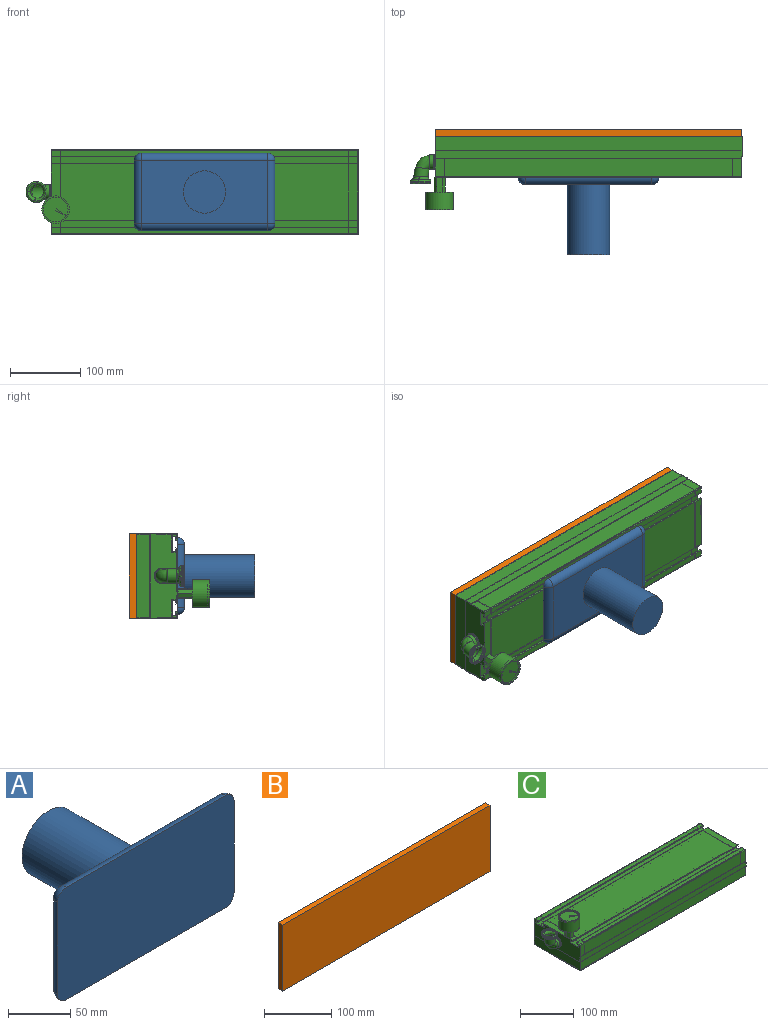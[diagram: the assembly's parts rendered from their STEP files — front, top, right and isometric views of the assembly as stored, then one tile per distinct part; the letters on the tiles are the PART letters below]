
ASSEMBLY  parts=3 mates=2
PART A: 12 faces, bbox 200x110x110 mm
  f0: plane 200x110mm, normal (0,-1,0), area 21914.2mm2, adj f4,f5,f6,f7,f8,f9,f10,f11
  f1: plane 180x90mm, normal (0,1,0), area 13372.6mm2, adj f2,f5,f6,f9,f10
  f2: cylinder r=30mm len=100mm, axis (0,-1,0), area 18849.6mm2, adj f1,f3
  f3: plane 60x60mm, normal (0,1,0), area 2827.4mm2, adj f2
  f4: sphere r=10mm, area 157.1mm2, adj f0,f5,f6
  f5: cylinder r=10mm len=90mm, axis (0,0,-1), area 1413.7mm2, adj f0,f1,f4,f7
  f6: cylinder r=10mm len=180mm, axis (1,0,0), area 2827.4mm2, adj f0,f1,f4,f8
  f7: sphere r=10mm, area 157.1mm2, adj f0,f5,f9
  f8: sphere r=10mm, area 157.1mm2, adj f0,f6,f10
  f9: cylinder r=10mm len=180mm, axis (-1,0,0), area 2827.4mm2, adj f0,f1,f7,f11
  f10: cylinder r=10mm len=90mm, axis (0,0,1), area 1413.7mm2, adj f0,f1,f8,f11
  f11: sphere r=10mm, area 157.1mm2, adj f0,f9,f10
PART B: 6 faces, bbox 435x10x120 mm
  f0: plane 435x10mm, normal (0,0,-1), area 4350mm2, adj f1,f3,f4,f5
  f1: plane 120x10mm, normal (1,0,0), area 1200mm2, adj f0,f2,f4,f5
  f2: plane 435x10mm, normal (0,0,1), area 4350mm2, adj f1,f3,f4,f5
  f3: plane 120x10mm, normal (-1,0,0), area 1200mm2, adj f0,f2,f4,f5
  f4: plane 435x120mm, normal (0,-1,0), area 52200mm2, adj f0,f1,f2,f3
  f5: plane 435x120mm, normal (0,1,0), area 52200mm2, adj f0,f1,f2,f3
PART C: 229 faces, bbox 472.5x122x104.6 mm
  f0: torus R=10mm, axis (0,1,0), area 808.9mm2, adj f5,f6
  f1: torus R=12.85mm, axis (0,0,1), area 133.1mm2, adj f4,f8
  f2: torus R=12mm, axis (1,0,0), area 148.1mm2, adj f5,f7
  f3: bspline ~13.12x11.53mm, area 103.6mm2, adj f6,f225,f226,f227
  f4: cylinder r=13.85mm len=27.7mm, axis (0,0,-1), area 117.2mm2, adj f1,f227,f228
  f5: cylinder r=9mm len=18mm, axis (1,0,0), area 326.2mm2, adj f0,f2
  f6: cylinder r=9mm len=19.81mm, axis (-0.14,0,0.99), area 692.2mm2, adj f0,f3,f225,f226
  f7: cylinder r=10mm len=20mm, axis (1,0,0), area 94mm2, adj f2,f126
  f8: cylinder r=12.85mm len=25.7mm, axis (0,0,1), area 80.7mm2, adj f1,f10
  f9: cylinder r=18.5mm len=37mm, axis (0,0,-1), area 2382.9mm2, adj f138,f204
  f10: torus R=12.85mm, axis (0,0,1), area 278.8mm2, adj f8,f13
  f11: torus R=12mm, axis (1,0,0), area 136.1mm2, adj f14,f16
  f12: bspline ~13.39x11.55mm, area 92.1mm2, adj f15,f122,f123,f124
  f13: cylinder r=14.85mm len=29.7mm, axis (0,0,-1), area 127.2mm2, adj f10,f124,f125
  f14: cylinder r=10mm len=20mm, axis (1,0,0), area 362.4mm2, adj f11,f121
  f15: cylinder r=10mm len=21.79mm, axis (-0.14,0,0.99), area 769.1mm2, adj f12,f121,f122,f123
  f16: cylinder r=11mm len=22mm, axis (1,0,0), area 69.1mm2, adj f11,f19
  f17: cylinder r=17.55mm len=35.1mm, axis (0,0,1), area 275.7mm2, adj f31,f98
  f18: cylinder r=19.5mm len=39mm, axis (0,0,-1), area 3063.1mm2, adj f97,f98
  f19: plane 121.1x38.6mm, normal (-1,0,0), area 4001.3mm2, adj f16,f22,f24,f28,f32,f33,f51,f52
  f20: plane 120.2x26.6mm, normal (1,0,0), area 24.8mm2, adj f23,f24,f27,f28,f32,f33,f34,f35
  f21: plane 120.2x26.6mm, normal (-1,0,0), area 24.8mm2, adj f23,f25,f27,f29,f34,f35,f36,f37
  f22: plane 120.15x0.1mm, normal (0,0,1), area 12mm2, adj f19,f85,f86,f110
  f23: plane 409.5x25mm, normal (0,1,0), area 10237.5mm2, adj f20,f21,f103,f113
  f24: plane 28.1x13mm, normal (0,1,0), area 328.2mm2, adj f19,f20,f105,f113,f117
  f25: plane 27.33x13mm, normal (0,1,0), area 328mm2, adj f21,f26,f108,f113,f118
  f26: plane 121.1x38.6mm, normal (1,0,0), area 4381.4mm2, adj f25,f29,f30,f67,f68,f69,f70,f71
  f27: plane 409.5x25mm, normal (0,-1,0), area 10237.5mm2, adj f20,f21,f104,f109
  f28: plane 27.33x13mm, normal (0,-1,0), area 328mm2, adj f19,f20,f106,f109,f120
  f29: plane 28.1x13mm, normal (0,-1,0), area 328.2mm2, adj f21,f26,f107,f109,f119
  f30: plane 120.15x0.1mm, normal (0,0,1), area 12mm2, adj f26,f84,f87,f116
  f31: plane 35.1x35.1mm, normal (0,0,1), area 942.1mm2, adj f17,f99,f100,f101
  f32: plane 62.26x13mm, normal (0,0,1), area 764.5mm2, adj f19,f20,f59,f91,f92,f93
  f33: plane 13x12.26mm, normal (0,0,1), area 114.5mm2, adj f19,f20,f58,f90,f94,f95
  f34: plane 409.5x79.8mm, normal (0,0,1), area 32678.1mm2, adj f20,f21,f37,f45
  f35: plane 409.5x8.4mm, normal (0,0,1), area 3439.8mm2, adj f20,f21,f46,f104
  f36: plane 409.5x8.4mm, normal (0,0,1), area 3439.8mm2, adj f20,f21,f43,f103
  f37: plane 409.5x2.5mm, normal (0,1,0), area 1023.8mm2, adj f20,f21,f34,f38
  f38: plane 409.5x5.15mm, normal (0,0,-1), area 2108.9mm2, adj f20,f21,f37,f39
  f39: plane 409.5x5.2mm, normal (0,0.99,-0.14), area 2151.4mm2, adj f20,f21,f38,f40
  f40: plane 409.5x22mm, normal (0,0,1), area 9009mm2, adj f20,f21,f39,f41
  f41: plane 409.5x5.2mm, normal (0,-0.99,-0.14), area 2151.4mm2, adj f20,f21,f40,f42
  f42: plane 409.5x5.15mm, normal (0,0,-1), area 2108.9mm2, adj f20,f21,f41,f43
  f43: plane 409.5x2.5mm, normal (0,-1,0), area 1023.8mm2, adj f20,f21,f36,f42
  f44: plane 409.5x5.15mm, normal (0,0,-1), area 2108.9mm2, adj f20,f21,f45,f50
  f45: plane 409.5x2.5mm, normal (0,-1,0), area 1023.8mm2, adj f20,f21,f34,f44
  f46: plane 409.5x2.5mm, normal (0,1,0), area 1023.8mm2, adj f20,f21,f35,f47
  f47: plane 409.5x5.15mm, normal (0,0,-1), area 2108.9mm2, adj f20,f21,f46,f48
  f48: plane 409.5x5.2mm, normal (0,0.99,-0.14), area 2151.4mm2, adj f20,f21,f47,f49
  f49: plane 409.5x22mm, normal (0,0,1), area 9009mm2, adj f20,f21,f48,f50
  f50: plane 409.5x5.2mm, normal (0,-0.99,-0.14), area 2151.4mm2, adj f20,f21,f44,f49
  f51: plane 13x8.6mm, normal (0,0,1), area 111.8mm2, adj f19,f20,f52,f106
  f52: plane 13x2.7mm, normal (0,1,0), area 35.1mm2, adj f19,f20,f51,f53
  f53: plane 13x5.16mm, normal (0,0,-1), area 67.1mm2, adj f19,f20,f52,f54
  f54: plane 13x5mm, normal (0,0.99,-0.14), area 65.7mm2, adj f19,f20,f53,f55
  f55: plane 21.77x13mm, normal (0,0,1), area 283mm2, adj f19,f20,f54,f56
  f56: plane 13x5mm, normal (0,-0.99,-0.14), area 65.7mm2, adj f19,f20,f55,f57
  f57: plane 13x5.16mm, normal (0,0,-1), area 67.1mm2, adj f19,f20,f56,f58
  f58: plane 13x2.7mm, normal (0,-1,0), area 35.1mm2, adj f19,f20,f33,f57
  f59: plane 13x2.7mm, normal (0,1,0), area 35.1mm2, adj f19,f20,f32,f60
  f60: plane 13x5.16mm, normal (0,0,-1), area 67.1mm2, adj f19,f20,f59,f61
  f61: plane 13x5mm, normal (0,0.99,-0.14), area 65.7mm2, adj f19,f20,f60,f62
  f62: plane 21.77x13mm, normal (0,0,1), area 283mm2, adj f19,f20,f61,f63
  f63: plane 13x5mm, normal (0,-0.99,-0.14), area 65.7mm2, adj f19,f20,f62,f64
  f64: plane 13x5.16mm, normal (0,0,-1), area 67.1mm2, adj f19,f20,f63,f65
  f65: plane 13x2.7mm, normal (0,-1,0), area 35.1mm2, adj f19,f20,f64,f66
  f66: plane 13x8.6mm, normal (0,0,1), area 111.8mm2, adj f19,f20,f65,f105
  f67: plane 13x8.6mm, normal (0,0,1), area 111.8mm2, adj f21,f26,f68,f108
  f68: plane 13x2.7mm, normal (0,-1,0), area 35.1mm2, adj f21,f26,f67,f69
  f69: plane 13x5.16mm, normal (0,0,-1), area 67.1mm2, adj f21,f26,f68,f70
  f70: plane 13x5mm, normal (0,-0.99,-0.14), area 65.7mm2, adj f21,f26,f69,f71
  f71: plane 21.77x13mm, normal (0,0,1), area 283mm2, adj f21,f26,f70,f72
  f72: plane 13x5mm, normal (0,0.99,-0.14), area 65.7mm2, adj f21,f26,f71,f73
  f73: plane 13x5.16mm, normal (0,0,-1), area 67.1mm2, adj f21,f26,f72,f74
  f74: plane 13x2.7mm, normal (0,1,0), area 35.1mm2, adj f21,f26,f73,f75
  f75: plane 80x13mm, normal (0,0,1), area 1040mm2, adj f21,f26,f74,f76
  f76: plane 13x2.7mm, normal (0,-1,0), area 35.1mm2, adj f21,f26,f75,f77
  f77: plane 13x5.16mm, normal (0,0,-1), area 67.1mm2, adj f21,f26,f76,f78
  f78: plane 13x5mm, normal (0,-0.99,-0.14), area 65.7mm2, adj f21,f26,f77,f79
  f79: plane 21.77x13mm, normal (0,0,1), area 283mm2, adj f21,f26,f78,f80
  f80: plane 13x5mm, normal (0,0.99,-0.14), area 65.7mm2, adj f21,f26,f79,f81
  f81: plane 13x5.16mm, normal (0,0,-1), area 67.1mm2, adj f21,f26,f80,f82
  f82: plane 13x2.7mm, normal (0,1,0), area 35.1mm2, adj f21,f26,f81,f83
  f83: plane 13x8.6mm, normal (0,0,1), area 111.8mm2, adj f21,f26,f82,f107
  f84: plane 435.7x20mm, normal (0,-1,0), area 8714mm2, adj f30,f85,f87,f88,f111
  f85: plane 121.15x29mm, normal (-1,0,0), area 2415mm2, adj f22,f84,f86,f88,f110,f111,f112,f120
  f86: plane 435.7x20mm, normal (0,1,0), area 8714mm2, adj f22,f85,f87,f88,f114
  f87: plane 121.15x29mm, normal (1,0,0), area 2415mm2, adj f30,f84,f86,f88,f114,f115,f116,f118
  f88: plane 435.7x120.3mm, normal (0,0,-1), area 52414.7mm2, adj f84,f85,f86,f87
  f89: plane 5.48x1.58mm, normal (0,0,-1), area 4.3mm2, adj f20,f90,f91
  f90: plane 21x7mm, normal (0.87,-0.5,0), area 169.7mm2, adj f33,f89,f91,f95,f97
  f91: plane 21x7mm, normal (0.87,0.5,0), area 169.7mm2, adj f32,f89,f90,f92,f97
  f92: plane 21x8.08mm, normal (0,1,0), area 169.7mm2, adj f32,f91,f93,f97
  f93: plane 21x7mm, normal (-0.87,0.5,0), area 169.7mm2, adj f32,f92,f94,f96,f97
  f94: plane 21x7mm, normal (-0.87,-0.5,0), area 169.7mm2, adj f33,f93,f95,f96,f97
  f95: plane 21x8.08mm, normal (0,-1,0), area 169.7mm2, adj f33,f90,f94,f97
  f96: plane 5.48x1.58mm, normal (0,0,-1), area 4.3mm2, adj f19,f93,f94
  f97: plane 39x39mm, normal (0,0,-1), area 1024.8mm2, adj f18,f90,f91,f92,f93,f94,f95
  f98: plane 39x39mm, normal (0,0,1), area 227mm2, adj f17,f18
  f99: plane 13.97x9.81mm, normal (0.57,0.82,0), area 17.1mm2, adj f31,f100,f101,f102
  f100: plane 2.6x1.5mm, normal (-0.87,0.5,0), area 3mm2, adj f31,f99,f101,f102
  f101: plane 15.47x7.21mm, normal (-0.42,-0.91,0), area 17.1mm2, adj f31,f99,f100,f102
  f102: plane 15.47x9.81mm, normal (0,0,1), area 25.5mm2, adj f99,f100,f101
  f103: cylinder r=1.5mm len=409.5mm, axis (-1,0,0), area 964.9mm2, adj f20,f21,f23,f36
  f104: cylinder r=1.5mm len=409.5mm, axis (-1,0,0), area 964.9mm2, adj f20,f21,f27,f35
  f105: cylinder r=1.5mm len=13mm, axis (1,0,0), area 30.6mm2, adj f19,f20,f24,f66
  f106: cylinder r=1.5mm len=13mm, axis (1,0,0), area 30.6mm2, adj f19,f20,f28,f51
  f107: cylinder r=1.5mm len=13mm, axis (-1,0,0), area 30.6mm2, adj f21,f26,f29,f83
  f108: cylinder r=1.5mm len=13mm, axis (-1,0,0), area 30.6mm2, adj f21,f25,f26,f67
  f109: plane 429.6x1mm, normal (0,0,1), area 427.6mm2, adj f20,f21,f27,f28,f29,f112,f119,f120
  f110: plane 9.77x0.1mm, normal (0,1,0), area 1mm2, adj f19,f22,f85,f120
  f111: plane 435.6x0.85mm, normal (0,0,-1), area 370.3mm2, adj f26,f84,f85,f112
  f112: plane 435.6x12mm, normal (0,-1,0), area 5223.3mm2, adj f26,f85,f109,f111,f119,f120
  f113: plane 429.6x1mm, normal (0,0,1), area 427.6mm2, adj f20,f21,f23,f24,f25,f115,f117,f118
  f114: plane 435.6x0.85mm, normal (0,0,-1), area 370.3mm2, adj f19,f86,f87,f115
  f115: plane 435.6x12mm, normal (0,1,0), area 5223.3mm2, adj f19,f87,f113,f114,f117,f118
  f116: plane 9.77x0.1mm, normal (0,-1,0), area 1mm2, adj f26,f30,f87,f118
  f117: cylinder r=3mm len=3mm, axis (0,1,0), area 4.2mm2, adj f19,f24,f113,f115
  f118: cylinder r=3mm len=3mm, axis (0,-1,0), area 4.3mm2, adj f25,f26,f87,f113,f115,f116
  f119: cylinder r=3mm len=3mm, axis (0,-1,0), area 4.2mm2, adj f26,f29,f109,f112
  f120: cylinder r=3mm len=3mm, axis (0,1,0), area 4.3mm2, adj f19,f28,f85,f109,f110,f112
  f121: torus R=10mm, axis (0,1,0), area 875.4mm2, adj f14,f15
  f122: bspline ~13.39x11.55mm, area 92.1mm2, adj f12,f15,f123,f124
  f123: bspline ~27.36x16.46mm, area 249.4mm2, adj f12,f15,f122,f125
  f124: bspline ~29.12x12.18mm, area 103.8mm2, adj f12,f13,f122,f125
  f125: bspline ~29.69x17.76mm, area 121.5mm2, adj f13,f123,f124
  f126: plane 120x40.6mm, normal (1,0,0), area 3933.5mm2, adj f7,f129,f131,f135,f139,f140,f158,f159
  f127: plane 118.2x28.6mm, normal (-1,0,0), area 34.6mm2, adj f130,f131,f134,f135,f139,f140,f141,f142
  f128: plane 118.2x26.6mm, normal (1,0,0), area 24.7mm2, adj f130,f132,f134,f136,f141,f142,f143,f144
  f129: plane 118.3x0.1mm, normal (0,0,-1), area 11.8mm2, adj f126,f191,f192,f193
  f130: plane 411.5x26mm, normal (0,-1,0), area 10699mm2, adj f127,f128,f209,f218
  f131: plane 28.1x11mm, normal (0,-1,0), area 288mm2, adj f126,f127,f211,f218,f221
  f132: plane 27.48x11mm, normal (0,-1,0), area 287.8mm2, adj f128,f133,f214,f218,f222
  f133: plane 120x38.6mm, normal (-1,0,0), area 4237.8mm2, adj f132,f136,f137,f174,f175,f176,f177,f178
  f134: plane 411.5x26mm, normal (0,1,0), area 10699mm2, adj f127,f128,f210,f215
  f135: plane 27.48x11mm, normal (0,1,0), area 287.8mm2, adj f126,f127,f212,f215,f224
  f136: plane 28.1x11mm, normal (0,1,0), area 288mm2, adj f128,f133,f213,f215,f223
  f137: plane 118.3x0.1mm, normal (0,0,-1), area 11.8mm2, adj f133,f191,f193,f194
  f138: plane 37x37mm, normal (0,0,-1), area 1073.3mm2, adj f9,f205,f206,f207
  f139: plane 61.53x11mm, normal (0,0,-1), area 645.2mm2, adj f126,f127,f166,f198,f199,f200
  f140: plane 11.53x11mm, normal (0,0,-1), area 95.2mm2, adj f126,f127,f165,f197,f201,f202
  f141: plane 411.5x77.8mm, normal (0,0,-1), area 32014.7mm2, adj f127,f128,f144,f152
  f142: plane 411.5x7.4mm, normal (0,0,-1), area 3045.1mm2, adj f127,f128,f153,f210
  f143: plane 411.5x7.4mm, normal (0,0,-1), area 3045.1mm2, adj f127,f128,f150,f209
  f144: plane 411.5x0.5mm, normal (0,-1,0), area 205.8mm2, adj f127,f128,f141,f145
  f145: plane 411.5x5.02mm, normal (0,0,1), area 2064.1mm2, adj f127,f128,f144,f146
  f146: plane 411.5x7.2mm, normal (0,-0.99,0.14), area 2993.5mm2, adj f127,f128,f145,f147
  f147: plane 411.5x24.31mm, normal (0,0,-1), area 10003.2mm2, adj f127,f128,f146,f148
  f148: plane 411.5x7.2mm, normal (0,0.99,0.14), area 2993.5mm2, adj f127,f128,f147,f149
  f149: plane 411.5x5.02mm, normal (0,0,1), area 2064.1mm2, adj f127,f128,f148,f150
  f150: plane 411.5x0.5mm, normal (0,1,0), area 205.8mm2, adj f127,f128,f143,f149
  f151: plane 411.5x5.02mm, normal (0,0,1), area 2064.1mm2, adj f127,f128,f152,f157
  f152: plane 411.5x0.5mm, normal (0,1,0), area 205.8mm2, adj f127,f128,f141,f151
  f153: plane 411.5x0.5mm, normal (0,-1,0), area 205.8mm2, adj f127,f128,f142,f154
  f154: plane 411.5x5.02mm, normal (0,0,1), area 2064.1mm2, adj f127,f128,f153,f155
  f155: plane 411.5x7.2mm, normal (0,-0.99,0.14), area 2993.5mm2, adj f127,f128,f154,f156
  f156: plane 411.5x24.31mm, normal (0,0,-1), area 10003.2mm2, adj f127,f128,f155,f157
  f157: plane 411.5x7.2mm, normal (0,0.99,0.14), area 2993.5mm2, adj f127,f128,f151,f156
  f158: plane 11x7.6mm, normal (0,0,-1), area 83.6mm2, adj f126,f127,f159,f212
  f159: plane 11x0.7mm, normal (0,-1,0), area 7.7mm2, adj f126,f127,f158,f160
  f160: plane 11x5.03mm, normal (0,0,1), area 55.3mm2, adj f126,f127,f159,f161
  f161: plane 11x7mm, normal (0,-0.99,0.14), area 77.8mm2, adj f126,f127,f160,f162
  f162: plane 24.08x11mm, normal (0,0,-1), area 264.9mm2, adj f126,f127,f161,f163
  f163: plane 11x7mm, normal (0,0.99,0.14), area 77.8mm2, adj f126,f127,f162,f164
  f164: plane 11x5.03mm, normal (0,0,1), area 55.3mm2, adj f126,f127,f163,f165
  f165: plane 11x0.7mm, normal (0,1,0), area 7.7mm2, adj f126,f127,f140,f164
  f166: plane 11x0.7mm, normal (0,-1,0), area 7.7mm2, adj f126,f127,f139,f167
  f167: plane 11x5.03mm, normal (0,0,1), area 55.3mm2, adj f126,f127,f166,f168
  f168: plane 11x7mm, normal (0,-0.99,0.14), area 77.8mm2, adj f126,f127,f167,f169
  f169: plane 24.08x11mm, normal (0,0,-1), area 264.9mm2, adj f126,f127,f168,f170
  f170: plane 11x7mm, normal (0,0.99,0.14), area 77.8mm2, adj f126,f127,f169,f171
  f171: plane 11x5.03mm, normal (0,0,1), area 55.3mm2, adj f126,f127,f170,f172
  f172: plane 11x0.7mm, normal (0,1,0), area 7.7mm2, adj f126,f127,f171,f173
  f173: plane 11x7.6mm, normal (0,0,-1), area 83.6mm2, adj f126,f127,f172,f211
  f174: plane 11x7.6mm, normal (0,0,-1), area 83.6mm2, adj f128,f133,f175,f214
  f175: plane 11x0.7mm, normal (0,1,0), area 7.7mm2, adj f128,f133,f174,f176
  f176: plane 11x5.03mm, normal (0,0,1), area 55.3mm2, adj f128,f133,f175,f177
  f177: plane 11x7mm, normal (0,0.99,0.14), area 77.8mm2, adj f128,f133,f176,f178
  f178: plane 24.08x11mm, normal (0,0,-1), area 264.9mm2, adj f128,f133,f177,f179
  f179: plane 11x7mm, normal (0,-0.99,0.14), area 77.8mm2, adj f128,f133,f178,f180
  f180: plane 11x5.03mm, normal (0,0,1), area 55.3mm2, adj f128,f133,f179,f181
  f181: plane 11x0.7mm, normal (0,-1,0), area 7.7mm2, adj f128,f133,f180,f182
  f182: plane 78x11mm, normal (0,0,-1), area 858mm2, adj f128,f133,f181,f183
  f183: plane 11x0.7mm, normal (0,1,0), area 7.7mm2, adj f128,f133,f182,f184
  f184: plane 11x5.03mm, normal (0,0,1), area 55.3mm2, adj f128,f133,f183,f185
  f185: plane 11x7mm, normal (0,0.99,0.14), area 77.8mm2, adj f128,f133,f184,f186
  f186: plane 24.08x11mm, normal (0,0,-1), area 264.9mm2, adj f128,f133,f185,f187
  f187: plane 11x7mm, normal (0,-0.99,0.14), area 77.8mm2, adj f128,f133,f186,f188
  f188: plane 11x5.03mm, normal (0,0,1), area 55.3mm2, adj f128,f133,f187,f189
  f189: plane 11x0.7mm, normal (0,-1,0), area 7.7mm2, adj f128,f133,f188,f190
  f190: plane 11x7.6mm, normal (0,0,-1), area 83.6mm2, adj f128,f133,f189,f213
  f191: plane 433.7x20mm, normal (0,1,0), area 8673.6mm2, adj f126,f129,f133,f137,f192,f194,f195,f216
  f192: plane 118.3x18mm, normal (1,0,0), area 2129.4mm2, adj f129,f191,f193,f195
  f193: plane 433.7x20mm, normal (0,-1,0), area 8673.6mm2, adj f126,f129,f133,f137,f192,f194,f195,f219
  f194: plane 118.3x18mm, normal (-1,0,0), area 2129.4mm2, adj f137,f191,f193,f195
  f195: plane 433.7x118.3mm, normal (0,0,1), area 51306.7mm2, adj f191,f192,f193,f194
  f196: plane 4.95x1.43mm, normal (0,0,1), area 3.5mm2, adj f127,f197,f198
  f197: plane 23x6mm, normal (-0.87,0.5,0), area 153.6mm2, adj f127,f140,f196,f198,f202,f204
  f198: plane 23x6mm, normal (-0.87,-0.5,0), area 153.6mm2, adj f127,f139,f196,f197,f199,f204
  f199: plane 23x6.93mm, normal (0,-1,0), area 159.3mm2, adj f139,f198,f200,f204
  f200: plane 23x6mm, normal (0.87,-0.5,0), area 153.6mm2, adj f126,f139,f199,f201,f203,f204
  f201: plane 23x6mm, normal (0.87,0.5,0), area 153.6mm2, adj f126,f140,f200,f202,f203,f204
  f202: plane 23x6.93mm, normal (0,1,0), area 159.3mm2, adj f140,f197,f201,f204
  f203: plane 4.95x1.43mm, normal (0,0,1), area 3.5mm2, adj f126,f200,f201
  f204: plane 37x37mm, normal (0,0,1), area 950.5mm2, adj f9,f197,f198,f199,f200,f201,f202
  f205: plane 3.8x2.67mm, normal (-0.57,-0.82,0), area 4.6mm2, adj f138,f206,f207,f208
  f206: plane 1x0.71mm, normal (0.87,-0.5,0), area 0.8mm2, adj f138,f205,f207,f208
  f207: plane 4.21x1.96mm, normal (0.42,0.91,0), area 4.6mm2, adj f138,f205,f206,f208
  f208: plane 4.21x2.67mm, normal (0,0,-1), area 1.9mm2, adj f205,f206,f207
  f209: cylinder r=0.5mm len=411.5mm, axis (-1,0,0), area 323.2mm2, adj f127,f128,f130,f143
  f210: cylinder r=0.5mm len=411.5mm, axis (-1,0,0), area 323.2mm2, adj f127,f128,f134,f142
  f211: cylinder r=0.5mm len=11mm, axis (1,0,0), area 8.6mm2, adj f126,f127,f131,f173
  f212: cylinder r=0.5mm len=11mm, axis (1,0,0), area 8.6mm2, adj f126,f127,f135,f158
  f213: cylinder r=0.5mm len=11mm, axis (-1,0,0), area 8.6mm2, adj f128,f133,f136,f190
  f214: cylinder r=0.5mm len=11mm, axis (-1,0,0), area 8.6mm2, adj f128,f132,f133,f174
  f215: plane 429.6x1mm, normal (0,0,-1), area 427.8mm2, adj f127,f128,f134,f135,f136,f217,f223,f224
  f216: plane 433.5x0.85mm, normal (0,0,1), area 368.5mm2, adj f126,f133,f191,f217
  f217: plane 433.5x10mm, normal (0,1,0), area 4333.4mm2, adj f126,f133,f215,f216,f223,f224
  f218: plane 429.6x1mm, normal (0,0,-1), area 427.8mm2, adj f127,f128,f130,f131,f132,f220,f221,f222
  f219: plane 433.5x0.85mm, normal (0,0,1), area 368.5mm2, adj f126,f133,f193,f220
  f220: plane 433.5x10mm, normal (0,-1,0), area 4333.4mm2, adj f126,f133,f218,f219,f221,f222
  f221: cylinder r=2mm len=2mm, axis (0,1,0), area 2.8mm2, adj f126,f131,f218,f220
  f222: cylinder r=2mm len=1.9mm, axis (0,-1,0), area 2.3mm2, adj f132,f133,f218,f220
  f223: cylinder r=2mm len=2mm, axis (0,-1,0), area 2.8mm2, adj f133,f136,f215,f217
  f224: cylinder r=2mm len=1.9mm, axis (0,1,0), area 2.3mm2, adj f126,f135,f215,f217
  f225: bspline ~13.17x11.57mm, area 103.6mm2, adj f3,f6,f226,f227
  f226: bspline ~26.84x15.99mm, area 277.7mm2, adj f3,f6,f225,f228
  f227: bspline ~27.16x11.26mm, area 49.3mm2, adj f3,f4,f225,f228
  f228: bspline ~27.69x16.56mm, area 57.5mm2, adj f4,f226,f227
PLACE A rot(axis=(1,0,0),180deg) t=(-449.05,13.78,111.99)mm
PLACE B t=(-76.8,92.28,46.6)mm
PLACE C rot(axis=(1,0,0),90deg) t=(-76.8,62.28,46.6)mm
MATE fastened A.f2 <-> C.f34  axis (0,1,0) through (-76.8,23.78,46.6)mm
MATE planar C.f88 <-> B.f4  axis (0,1,0) through (-76.8,82.28,46.6)mm
